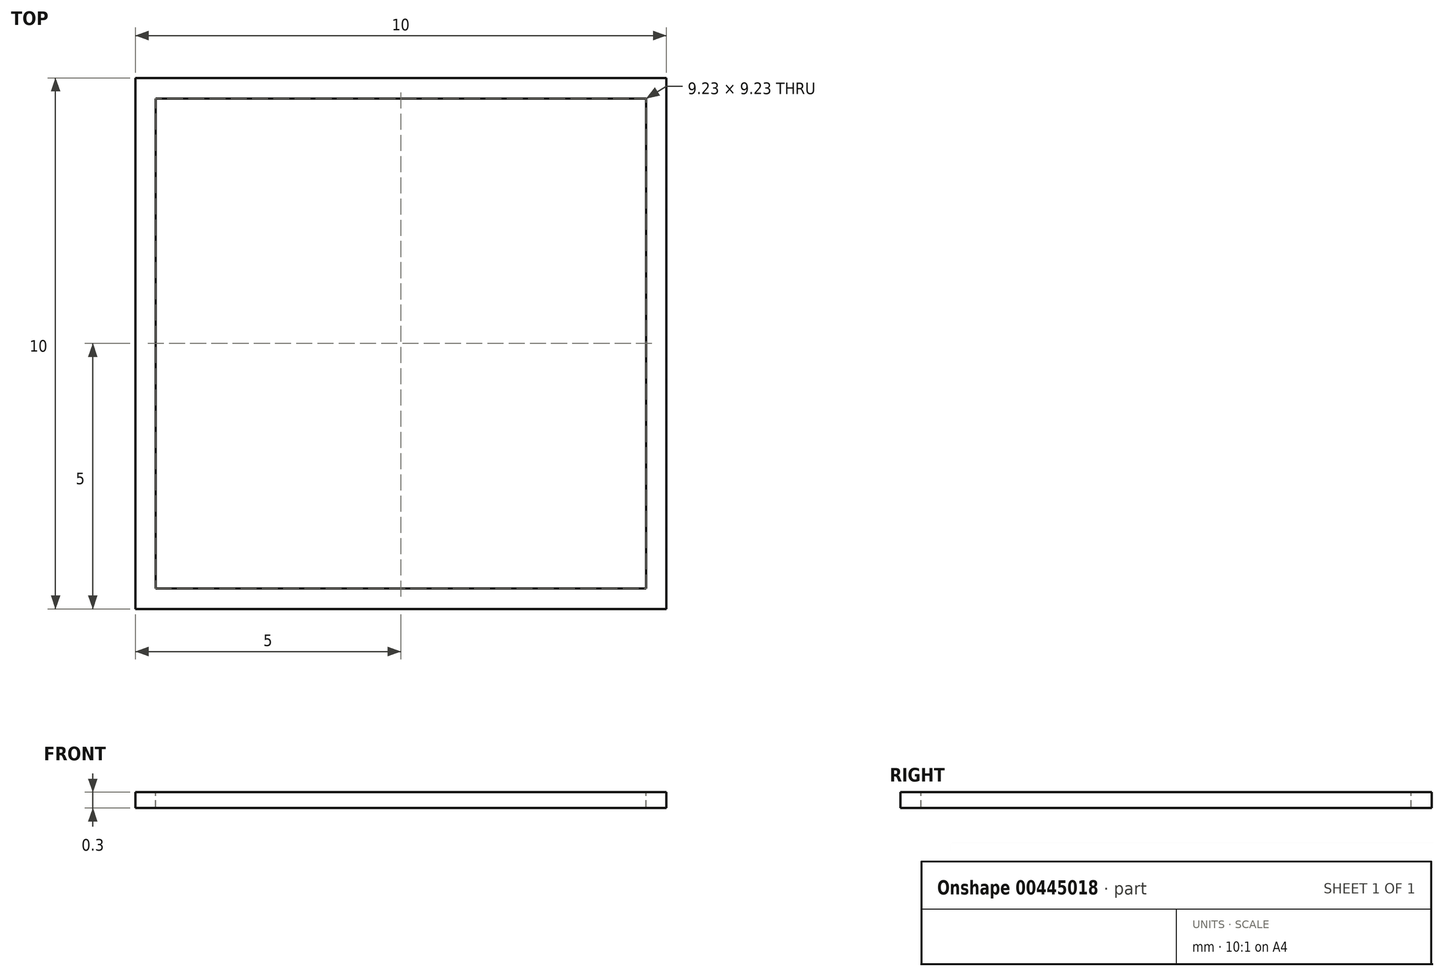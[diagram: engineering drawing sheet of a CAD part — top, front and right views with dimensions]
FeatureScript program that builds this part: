
annotation { "Feature Type Name" : "Feature", "Feature Type Description" : "" }
export const myFeature = defineFeature(function(context is Context, id is Id, definition is map)
    precondition{}
    {
        {
            var Q0;
            Q0=qCreatedBy(makeId("Top.planeOp"),FACE);
            var sketch = newSketch(context, id + "F0", { "sketchPlane" : qUnion([Q0])});
            skLineSegment(sketch, "E0.bottom", {"start": v(0, 0) * mm, "end": v(10, 0) * mm});
            skLineSegment(sketch, "E0.top", {"start": v(0, 10) * mm, "end": v(10, 10) * mm});
            skLineSegment(sketch, "E0.left", {"start": v(0, 0) * mm, "end": v(0, 10) * mm});
            skLineSegment(sketch, "E0.right", {"start": v(10, 0) * mm, "end": v(10, 10) * mm});
            skSolve(sketch);
        }
        {
            var Q0;
            Q0=makeQuery(id+"F0.imprint","IMPRINT",FACE,{"disambiguationData":[TD([[makeQuery(id+"F0.imprint","IMPRINT",EDGE,{"derivedFrom":sQuery(id+"F0.wireOp",EDGE,"E0.bottom")}),1.0]])]});
            extrude(context, id + "F1", {"entities" : qUnion([Q0]), "depth" : .3 * mm});
        }
        {
            var Q0;
            Q0=makeQuery(id+"F1.opExtrude","CAP_FACE",FACE,{"disambiguationData":[OSD([sQuery(id+"F0.wireOp",EDGE,"E0.bottom"),sQuery(id+"F0.wireOp",EDGE,"E0.top"),sQuery(id+"F0.wireOp",EDGE,"E0.left"),sQuery(id+"F0.wireOp",EDGE,"E0.right")])],"isStart":false});
            var sketch = newSketch(context, id + "F2", { "sketchPlane" : qUnion([Q0])});
            skLineSegment(sketch, "E1.bottom", {"start": v(0.38, 9.62) * mm, "end": v(9.62, 9.62) * mm});
            skLineSegment(sketch, "E1.top", {"start": v(0.38, 0.38) * mm, "end": v(9.62, 0.38) * mm});
            skLineSegment(sketch, "E1.left", {"start": v(0.38, 9.62) * mm, "end": v(0.38, 0.38) * mm});
            skLineSegment(sketch, "E1.right", {"start": v(9.62, 9.62) * mm, "end": v(9.62, 0.38) * mm});
            skPoint(sketch, "E1.middle", {"position": v(5, 5) * mm});
            skPoint(sketch, "E1.middle.positionSnap0", {"position": v(0, 5) * mm});
            skPoint(sketch, "E1.middle.positionSnap1", {"position": v(5, 10) * mm});
            skPoint(sketch, "E1.centerSnap0", {"position": v(0, 5) * mm});
            skPoint(sketch, "E1.centerSnap1", {"position": v(5, 10) * mm});
            skSolve(sketch);
        }
        {
            var Q0;
            Q0=makeQuery(id+"F2.imprint","IMPRINT",FACE,{"disambiguationData":[TD([[makeQuery(id+"F2.imprint","IMPRINT",EDGE,{"derivedFrom":sQuery(id+"F2.wireOp",EDGE,"E1.bottom")}),-1.0]])]});
            extrude(context, id + "F3", {"entities" : qUnion([Q0]), "operationType" : NewBodyOperationType.REMOVE, "oppositeDirection" : true, "depth" : 25.4 * mm});
        }
    });
